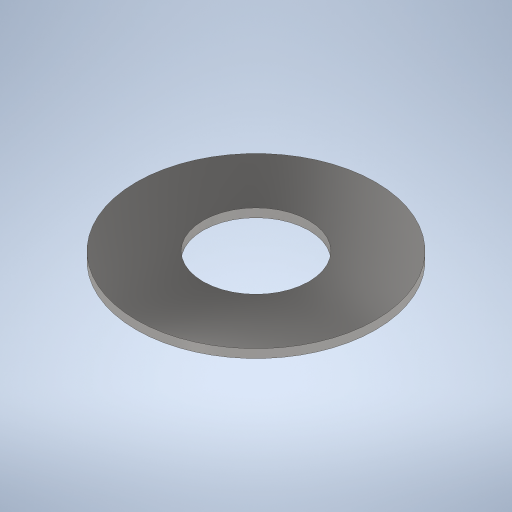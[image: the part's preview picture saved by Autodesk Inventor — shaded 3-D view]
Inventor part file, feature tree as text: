
AUTODESK INVENTOR PART (.ipt)
format: ipt  version: 2024.2 (Build 282272000, 272)  size: 246,784 bytes
history: native  units: mm
features: revolve x1, sketch x1
ambient origin geometry x8: Origin, YZ Plane, XZ Plane, XY Plane, X Axis, Y Axis, Z Axis, Center Point
bodies: Solid1 (feature_tree)
feature tree (2):
  revolve  "Revolution1"  [1 undecoded]
  sketch  "Sketch1"  dims[d5=90.0deg]
note: 1 required parameter value undecoded (feature->parameter linkage not recoverable at this tier; creation-order binding heuristic only, values carry confidence <= 0.55)
